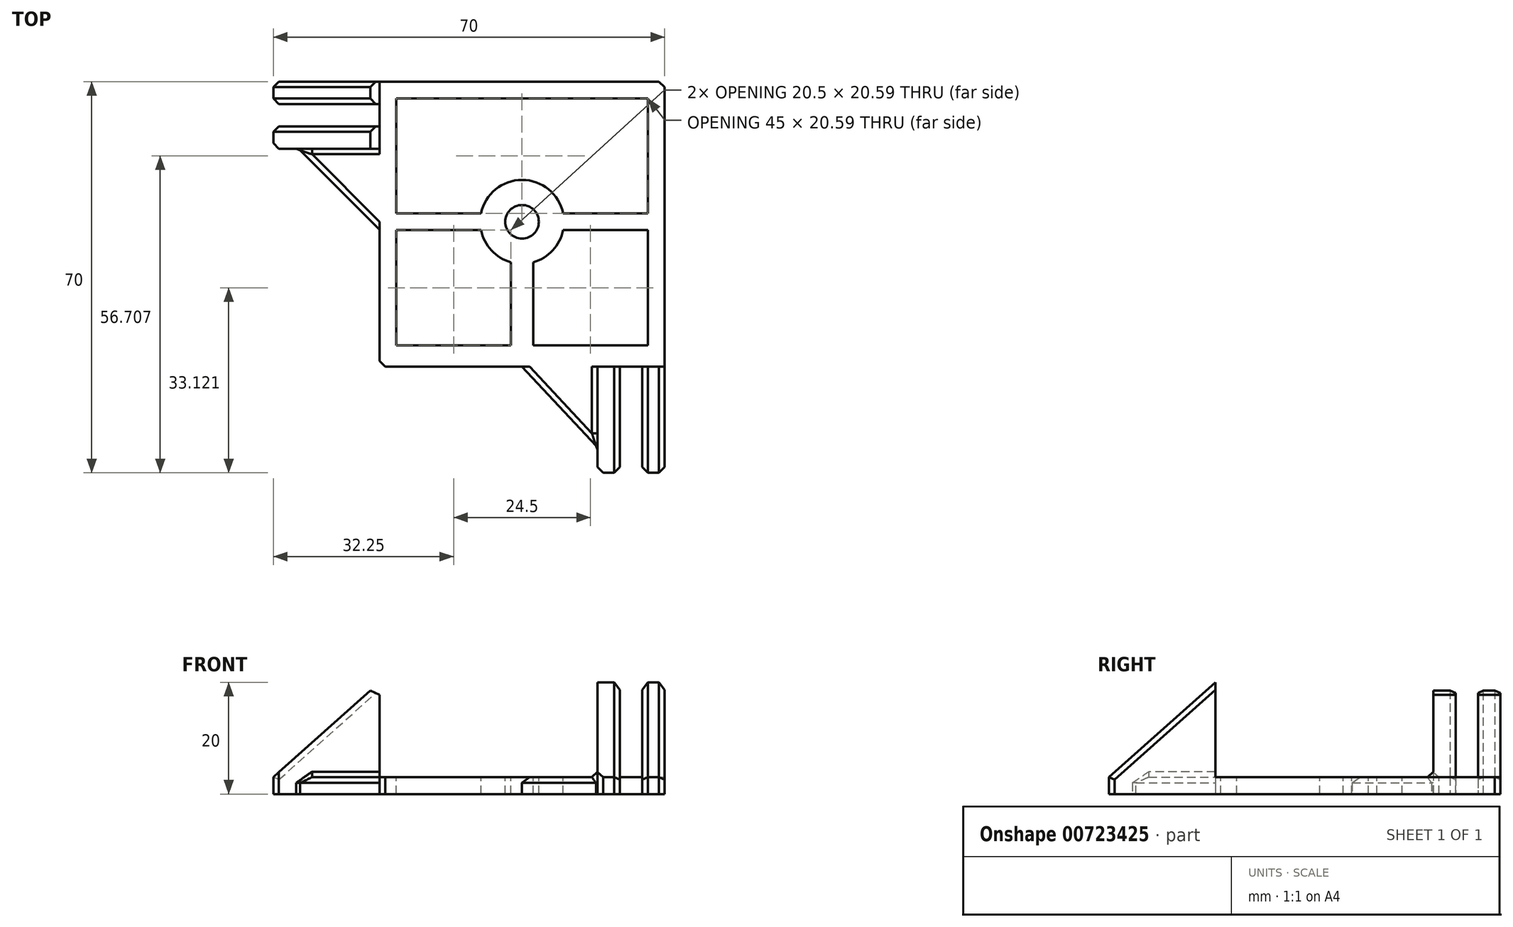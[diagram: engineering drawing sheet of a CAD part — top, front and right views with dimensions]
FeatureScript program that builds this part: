
annotation { "Feature Type Name" : "Feature", "Feature Type Description" : "" }
export const myFeature = defineFeature(function(context is Context, id is Id, definition is map)
    precondition{}
    {
        {
            var Q0;
            Q0=qCreatedBy(makeId("Top.planeOp"),FACE);
            var sketch = newSketch(context, id + "F0", { "sketchPlane" : qUnion([Q0])});
            skLineSegment(sketch, "E0.bottom", {"start": v(0, 0) * mm, "end": v(51, 0) * mm});
            skLineSegment(sketch, "E0.top", {"start": v(0, -51) * mm, "end": v(51, -51) * mm});
            skLineSegment(sketch, "E0.left", {"start": v(0, 0) * mm, "end": v(0, -51) * mm});
            skLineSegment(sketch, "E0.right", {"start": v(51, 0) * mm, "end": v(51, -51) * mm});
            skSolve(sketch);
        }
        {
            var Q0;
            Q0=qSketchRegion(id+"F0",true);
            extrude(context, id + "F1", {"entities" : qUnion([Q0]), "depth" : 3 * mm, "offsetDistance" : 25 * mm});
        }
        {
            var Q0;
            Q0=qCreatedBy(makeId("Top.planeOp"),FACE);
            var sketch = newSketch(context, id + "F2", { "sketchPlane" : qUnion([Q0])});
            skLineSegment(sketch, "E1", {"start": v(0, 0) * mm, "end": v(-19, 0) * mm});
            skLineSegment(sketch, "E2", {"start": v(-19, 0) * mm, "end": v(-19, -4) * mm});
            skLineSegment(sketch, "E3", {"start": v(-19, -4) * mm, "end": v(0, -4) * mm});
            skLineSegment(sketch, "E4", {"start": v(0, -4) * mm, "end": v(0, -8) * mm});
            skLineSegment(sketch, "E5", {"start": v(0, -8) * mm, "end": v(-19, -8) * mm});
            skLineSegment(sketch, "E6", {"start": v(-19, -8) * mm, "end": v(-19, -12) * mm});
            skLineSegment(sketch, "E7", {"start": v(-19, -12) * mm, "end": v(0, -12) * mm});
            skLineSegment(sketch, "E8", {"start": v(0, 0) * mm, "end": v(0, -12) * mm});
            skSolve(sketch);
        }
        {
            var Q0;
            Q0=qSketchRegion(id+"F2",true);
            extrude(context, id + "F3", {"entities" : qUnion([Q0]), "operationType" : NewBodyOperationType.ADD, "depth" : 20 * mm, "offsetDistance" : 25 * mm});
        }
        {
            var Q0;
            Q0=qCreatedBy(makeId("Top.planeOp"),FACE);
            var sketch = newSketch(context, id + "F4", { "sketchPlane" : qUnion([Q0])});
            skLineSegment(sketch, "E9", {"start": v(0, 0) * mm, "end": v(0, -11.5) * mm});
            skLineSegment(sketch, "E10", {"start": v(0, -11.5) * mm, "end": v(-15, -11.5) * mm});
            skLineSegment(sketch, "E11", {"start": v(0, -11.5) * mm, "end": v(0, -26.5) * mm});
            skLineSegment(sketch, "E12", {"start": v(0, -26.5) * mm, "end": v(-15, -11.5) * mm});
            skSolve(sketch);
        }
        {
            var Q0;
            Q0=makeQuery(id+"F4.imprint","IMPRINT",FACE,{"disambiguationData":[TD([[makeQuery(id+"F4.imprint","IMPRINT",EDGE,{"derivedFrom":sQuery(id+"F4.wireOp",EDGE,"E10")}),1.0]])]});
            extrude(context, id + "F5", {"entities" : qUnion([Q0]), "operationType" : NewBodyOperationType.ADD, "depth" : 3 * mm, "offsetDistance" : 25 * mm});
        }
        {
            var Q0;
            Q0=qCreatedBy(makeId("Top.planeOp"),FACE);
            var sketch = newSketch(context, id + "F6", { "sketchPlane" : qUnion([Q0])});
            skLineSegment(sketch, "E13", {"start": v(0, 0) * mm, "end": v(0, -51) * mm});
            skLineSegment(sketch, "E14", {"start": v(0, -51) * mm, "end": v(51, -51) * mm});
            skLineSegment(sketch, "E15", {"start": v(51, -51) * mm, "end": v(51, -70) * mm});
            skLineSegment(sketch, "E16", {"start": v(51, -70) * mm, "end": v(47, -70) * mm});
            skLineSegment(sketch, "E17", {"start": v(47, -70) * mm, "end": v(47, -51) * mm});
            skLineSegment(sketch, "E18", {"start": v(47, -51) * mm, "end": v(43, -51) * mm});
            skLineSegment(sketch, "E19", {"start": v(43, -51) * mm, "end": v(43, -70) * mm});
            skLineSegment(sketch, "E20", {"start": v(43, -70) * mm, "end": v(39, -70) * mm});
            skLineSegment(sketch, "E21", {"start": v(39, -70) * mm, "end": v(39, -51) * mm});
            skLineSegment(sketch, "E22", {"start": v(39, -51) * mm, "end": v(51, -51) * mm});
            skSolve(sketch);
        }
        {
            var Q0;
            Q0=qSketchRegion(id+"F6",true);
            extrude(context, id + "F7", {"entities" : qUnion([Q0]), "operationType" : NewBodyOperationType.ADD, "depth" : 20 * mm, "offsetDistance" : 25 * mm});
        }
        {
            var Q0;
            Q0=qCreatedBy(makeId("Top.planeOp"),FACE);
            var sketch = newSketch(context, id + "F8", { "sketchPlane" : qUnion([Q0])});
            skLineSegment(sketch, "E23", {"start": v(0, 0) * mm, "end": v(0, -51) * mm});
            skLineSegment(sketch, "E24", {"start": v(0, -51) * mm, "end": v(51, -51) * mm});
            skLineSegment(sketch, "E25", {"start": v(51, -51) * mm, "end": v(39.5, -51) * mm});
            skLineSegment(sketch, "E26", {"start": v(39.5, -51) * mm, "end": v(39.5, -66) * mm});
            skLineSegment(sketch, "E27", {"start": v(39.5, -66) * mm, "end": v(25.5, -51) * mm});
            skLineSegment(sketch, "E28", {"start": v(25.5, -51) * mm, "end": v(39.5, -51) * mm});
            skSolve(sketch);
        }
        {
            var Q0;
            Q0=qSketchRegion(id+"F8",true);
            extrude(context, id + "F9", {"entities" : qUnion([Q0]), "operationType" : NewBodyOperationType.ADD, "depth" : 3 * mm, "offsetDistance" : 25 * mm});
        }
        {
            var Q0;
            Q0=makeQuery(id+"F9.boolean.opBoolean","MERGE",FACE,{"derivedFrom":[makeQuery(id+"F5.boolean.opBoolean","MERGE",FACE,{"derivedFrom":[makeQuery(id+"F1.opExtrude","CAP_FACE",FACE,{"disambiguationData":[OSD([sQuery(id+"F0.wireOp",EDGE,"E0.bottom"),sQuery(id+"F0.wireOp",EDGE,"E0.top"),sQuery(id+"F0.wireOp",EDGE,"E0.left"),sQuery(id+"F0.wireOp",EDGE,"E0.right")])],"isStart":false}),makeQuery(id+"F5.opExtrude","CAP_FACE",FACE,{"disambiguationData":[OSD([sQuery(id+"F4.wireOp",EDGE,"E10"),sQuery(id+"F4.wireOp",EDGE,"E11"),sQuery(id+"F4.wireOp",EDGE,"E12")])],"isStart":false})]}),makeQuery(id+"F9.opExtrude","CAP_FACE",FACE,{"disambiguationData":[OSD([sQuery(id+"F8.wireOp",EDGE,"E26"),sQuery(id+"F8.wireOp",EDGE,"E27"),sQuery(id+"F8.wireOp",EDGE,"E28")])],"isStart":false})]});
            var sketch = newSketch(context, id + "F10", { "sketchPlane" : qUnion([Q0])});
            skCircle(sketch, "E29", {"center": v(25.5, -25.09) * mm, "radius": 3 * mm});
            skPoint(sketch, "E29.centerSnap0", {"position": v(25.5, 0) * mm});
            skSolve(sketch);
        }
        {
            var Q0;
            Q0 = qSketchRegion(id + "F10", true);
            extrude(context, id + "F11", {"entities" : qUnion([Q0]), "operationType" : NewBodyOperationType.REMOVE, "oppositeDirection" : true, "depth" : 25 * mm, "offsetDistance" : 25 * mm});
        }
        {
            var Q0;
            Q0=makeQuery(id+"F9.boolean.opBoolean","MERGE",FACE,{"derivedFrom":[makeQuery(id+"F5.boolean.opBoolean","MERGE",FACE,{"derivedFrom":[makeQuery(id+"F1.opExtrude","CAP_FACE",FACE,{"disambiguationData":[OSD([sQuery(id+"F0.wireOp",EDGE,"E0.bottom"),sQuery(id+"F0.wireOp",EDGE,"E0.top"),sQuery(id+"F0.wireOp",EDGE,"E0.left"),sQuery(id+"F0.wireOp",EDGE,"E0.right")])],"isStart":false}),makeQuery(id+"F5.opExtrude","CAP_FACE",FACE,{"disambiguationData":[OSD([sQuery(id+"F4.wireOp",EDGE,"E10"),sQuery(id+"F4.wireOp",EDGE,"E11"),sQuery(id+"F4.wireOp",EDGE,"E12")])],"isStart":false})]}),makeQuery(id+"F9.opExtrude","CAP_FACE",FACE,{"disambiguationData":[OSD([sQuery(id+"F8.wireOp",EDGE,"E26"),sQuery(id+"F8.wireOp",EDGE,"E27"),sQuery(id+"F8.wireOp",EDGE,"E28")])],"isStart":false})]});
            var sketch = newSketch(context, id + "F12", { "sketchPlane" : qUnion([Q0])});
            skCircle(sketch, "E30", {"center": v(25.5, -25.09) * mm, "radius": 7.5 * mm});
            skLineSegment(sketch, "E31", {"start": v(0, 0) * mm, "end": v(0, -3) * mm});
            skLineSegment(sketch, "E32", {"start": v(0, -3) * mm, "end": v(25.5, -3) * mm});
            skLineSegment(sketch, "E33", {"start": v(25.5, -3) * mm, "end": v(23.5, -3) * mm});
            skLineSegment(sketch, "E34", {"start": v(23.5, -3) * mm, "end": v(23.5, -17.86) * mm});
            skLineSegment(sketch, "E35", {"start": v(0, -3) * mm, "end": v(3, -3) * mm});
            skLineSegment(sketch, "E36", {"start": v(3, -3) * mm, "end": v(3, -25.09) * mm});
            skLineSegment(sketch, "E37", {"start": v(3, -25.09) * mm, "end": v(3, -23.59) * mm});
            skLineSegment(sketch, "E38", {"start": v(3, -23.59) * mm, "end": v(18.15, -23.59) * mm});
            skLineSegment(sketch, "E39", {"start": v(25.5, -25.09) * mm, "end": v(51, -25.09) * mm});
            skLineSegment(sketch, "E40", {"start": v(25.5, -25.09) * mm, "end": v(25.5, -51) * mm});
            skLineSegment(sketch, "E41.MirrorCS", {"start": v(3, -26.59) * mm, "end": v(18.15, -26.59) * mm});
            skLineSegment(sketch, "E42.MirrorCS", {"start": v(3, -47.17) * mm, "end": v(3, -25.09) * mm});
            skLineSegment(sketch, "E43.MirrorCS", {"start": v(0, -47.17) * mm, "end": v(25.5, -47.17) * mm});
            skLineSegment(sketch, "E44.MirrorCS", {"start": v(23.5, -47.17) * mm, "end": v(23.5, -32.31) * mm});
            skLineSegment(sketch, "E45.MirrorCS", {"start": v(27.5, -47.17) * mm, "end": v(27.5, -32.31) * mm});
            skLineSegment(sketch, "E46.MirrorCS", {"start": v(51, -47.17) * mm, "end": v(25.5, -47.17) * mm});
            skLineSegment(sketch, "E47.MirrorCS", {"start": v(48, -47.17) * mm, "end": v(48, -25.09) * mm});
            skLineSegment(sketch, "E48.MirrorCS", {"start": v(48, -26.59) * mm, "end": v(32.85, -26.59) * mm});
            skLineSegment(sketch, "E49.MirrorCS", {"start": v(48, -23.59) * mm, "end": v(32.85, -23.59) * mm});
            skLineSegment(sketch, "E50.MirrorCS", {"start": v(48, -3) * mm, "end": v(48, -25.09) * mm});
            skLineSegment(sketch, "E51.MirrorCS", {"start": v(51, -3) * mm, "end": v(25.5, -3) * mm});
            skLineSegment(sketch, "E52.MirrorCS", {"start": v(27.5, -3) * mm, "end": v(27.5, -17.86) * mm});
            skSolve(sketch);
        }
        {
            var Q0;
            {var subQ4=sQuery(id+"F12.wireOp",EDGE,"E49.MirrorCS");Q0=makeQuery(id+"F12.imprint","IMPRINT",FACE,{"disambiguationData":[TD([[makeQuery(id+"F12.imprint","IMPRINT",EDGE,{"derivedFrom":subQ4}),-1.0]])]});}
            var Q1;
            {var subQ4=sQuery(id+"F12.wireOp",EDGE,"E45.MirrorCS");Q1=makeQuery(id+"F12.imprint","IMPRINT",FACE,{"disambiguationData":[TD([[makeQuery(id+"F12.imprint","IMPRINT",EDGE,{"derivedFrom":subQ4}),-1.0]])]});}
            var Q2;
            Q2=makeQuery(id+"F12.imprint","IMPRINT",FACE,{"disambiguationData":[TD([[makeQuery(id+"F12.imprint","IMPRINT",EDGE,{"derivedFrom":sQuery(id+"F12.wireOp",EDGE,"E32")}),-1.0]])]});
            var Q3;
            {var subQ1=sQuery(id+"F12.wireOp",EDGE,"E41.MirrorCS");Q3=makeQuery(id+"F12.imprint","IMPRINT",FACE,{"disambiguationData":[TD([[makeQuery(id+"F12.imprint","IMPRINT",EDGE,{"derivedFrom":subQ1}),-1.0]])]});}
            extrude(context, id + "F13", {"entities" : qUnion([Q0, Q1, Q2, Q3]), "operationType" : NewBodyOperationType.REMOVE, "oppositeDirection" : true, "depth" : 25 * mm, "offsetDistance" : 25 * mm});
        }
        {
            var Q0;
            Q0=makeQuery(id+"F3.opExtrude","SWEPT_FACE",FACE,{"disambiguationData":[OSD([sQuery(id+"F2.wireOp",EDGE,"E7")])]});
            var sketch = newSketch(context, id + "F14", { "sketchPlane" : qUnion([Q0])});
            skLineSegment(sketch, "E53", {"start": v(-19, 3) * mm, "end": v(0, 20) * mm});
            skLineSegment(sketch, "E54", {"start": v(0, 20) * mm, "end": v(-19, 20) * mm});
            skLineSegment(sketch, "E55", {"start": v(-19, 20) * mm, "end": v(-19, 3) * mm});
            skSolve(sketch);
        }
        {
            var Q0;
            Q0 = qSketchRegion(id + "F14", true);
            extrude(context, id + "F15", {"entities" : qUnion([Q0]), "operationType" : NewBodyOperationType.REMOVE, "oppositeDirection" : true, "depth" : 25 * mm, "offsetDistance" : 25 * mm});
        }
        {
            var Q0;
            Q0=makeQuery(id+"F7.opExtrude","SWEPT_FACE",FACE,{"disambiguationData":[OSD([sQuery(id+"F6.wireOp",EDGE,"E21")])]});
            var sketch = newSketch(context, id + "F16", { "sketchPlane" : qUnion([Q0])});
            skLineSegment(sketch, "E56", {"start": v(70, 3) * mm, "end": v(51, 20) * mm});
            skLineSegment(sketch, "E57", {"start": v(51, 20) * mm, "end": v(70, 20) * mm});
            skLineSegment(sketch, "E58", {"start": v(70, 20) * mm, "end": v(70, 3) * mm});
            skSolve(sketch);
        }
        {
            var Q0;
            Q0 = qSketchRegion(id + "F16", true);
            extrude(context, id + "F17", {"entities" : qUnion([Q0]), "operationType" : NewBodyOperationType.REMOVE, "oppositeDirection" : true, "depth" : 25 * mm, "offsetDistance" : 25 * mm});
        }
        {
            var Q0;
            Q0 = qSketchRegion(id + "F16", true);
            extrude(context, id + "F18", {"entities" : qUnion([Q0]), "operationType" : NewBodyOperationType.REMOVE, "oppositeDirection" : true, "depth" : 25 * mm, "offsetDistance" : 25 * mm});
        }
        {
            var Q0;
            Q0=makeQuery(id+"F15.boolean.opBoolean","INTERSECT",EDGE,{"derivedFrom":[makeQuery(id+"F3.boolean.opBoolean","MERGE",FACE,{"derivedFrom":[makeQuery(id+"F1.opExtrude","SWEPT_FACE",FACE,{"disambiguationData":[OSD([sQuery(id+"F0.wireOp",EDGE,"E0.bottom")])]}),makeQuery(id+"F3.opExtrude","SWEPT_FACE",FACE,{"disambiguationData":[OSD([sQuery(id+"F2.wireOp",EDGE,"E1")])]})]}),makeQuery(id+"F15.opExtrude","SWEPT_FACE",FACE,{"disambiguationData":[OSD([sQuery(id+"F14.wireOp",EDGE,"E53")])]})]});
            var Q1;
            Q1=makeQuery(id+"F15.boolean.opBoolean","INTERSECT",EDGE,{"derivedFrom":[makeQuery(id+"F3.opExtrude","SWEPT_FACE",FACE,{"disambiguationData":[OSD([sQuery(id+"F2.wireOp",EDGE,"E3")])]}),makeQuery(id+"F15.opExtrude","SWEPT_FACE",FACE,{"disambiguationData":[OSD([sQuery(id+"F14.wireOp",EDGE,"E53")])]})]});
            var Q2;
            {var subQ0=sQuery(id+"F2.wireOp",EDGE,"E8");Q2=makeQuery(id+"F15.boolean.opBoolean","MERGE",EDGE,{"derivedFrom":[makeQuery(id+"F3.opExtrude","CAP_EDGE",EDGE,{"disambiguationData":[OSD([subQ0]),TDD([makeQuery(id+"F2.imprint","IMPRINT",EDGE,{"disambiguationData":[TD([[makeQuery(id+"F2.imprint","INTERSECT",VERTEX,{"derivedFrom":[sQuery(id+"F2.wireOp",EDGE,"E1"),subQ0]}),-1.0]])],"derivedFrom":subQ0})])],"isStart":false}),makeQuery(id+"F15.opExtrude","SWEPT_EDGE",EDGE,{"disambiguationData":[OSD([sQuery(id+"F2.wireOp",EDGE,"E7"),subQ0,sQuery(id+"F14.wireOp",EDGE,"E53"),sQuery(id+"F14.wireOp",EDGE,"E54")])]})]});}
            var Q3;
            {var subQ0=sQuery(id+"F2.wireOp",EDGE,"E8");var subQ1=sQuery(id+"F2.wireOp",EDGE,"E7");Q3=makeQuery(id+"F15.boolean.opBoolean","MERGE",EDGE,{"derivedFrom":[makeQuery(id+"F3.opExtrude","CAP_EDGE",EDGE,{"disambiguationData":[OSD([subQ0]),TDD([makeQuery(id+"F2.imprint","IMPRINT",EDGE,{"disambiguationData":[TD([[makeQuery(id+"F2.imprint","INTERSECT",VERTEX,{"derivedFrom":[sQuery(id+"F2.wireOp",EDGE,"E5"),subQ0]}),-1.0]])],"derivedFrom":subQ0})])],"isStart":false}),makeQuery(id+"F15.opExtrude","SWEPT_EDGE",EDGE,{"disambiguationData":[OSD([subQ1,subQ0,sQuery(id+"F14.wireOp",EDGE,"E53"),sQuery(id+"F14.wireOp",EDGE,"E54")])]})]});}
            var Q4;
            Q4=makeQuery(id+"F15.boolean.opBoolean","INTERSECT",EDGE,{"derivedFrom":[makeQuery(id+"F3.opExtrude","SWEPT_FACE",FACE,{"disambiguationData":[OSD([sQuery(id+"F2.wireOp",EDGE,"E5")])]}),makeQuery(id+"F15.opExtrude","SWEPT_FACE",FACE,{"disambiguationData":[OSD([sQuery(id+"F14.wireOp",EDGE,"E53")])]})]});
            var Q5;
            Q5=makeQuery(id+"F15.boolean.opBoolean","COPY",EDGE,{"derivedFrom":makeQuery(id+"F15.opExtrude","CAP_EDGE",EDGE,{"disambiguationData":[OSD([sQuery(id+"F14.wireOp",EDGE,"E53")])],"isStart":true})});
            var Q6;
            {var subQ0=sQuery(id+"F2.wireOp",EDGE,"E6");var subQ1=sQuery(id+"F14.wireOp",EDGE,"E53");Q6=makeQuery(id+"F15.boolean.opBoolean","COPY",EDGE,{"disambiguationData":[topologyDisambiguationEdgeConnected([makeQuery(id+"F3.opExtrude","SWEPT_FACE",FACE,{"disambiguationData":[OSD([subQ0])]})])],"derivedFrom":makeQuery(id+"F15.opExtrude","SWEPT_EDGE",EDGE,{"disambiguationData":[OSD([subQ0,sQuery(id+"F2.wireOp",EDGE,"E7"),subQ1,sQuery(id+"F14.wireOp",EDGE,"E55")])]})});}
            var Q7;
            {var subQ0=sQuery(id+"F14.wireOp",EDGE,"E53");Q7=makeQuery(id+"F15.boolean.opBoolean","COPY",EDGE,{"disambiguationData":[topologyDisambiguationEdgeConnected([makeQuery(id+"F3.opExtrude","SWEPT_FACE",FACE,{"disambiguationData":[OSD([sQuery(id+"F2.wireOp",EDGE,"E2")])]})])],"derivedFrom":makeQuery(id+"F15.opExtrude","SWEPT_EDGE",EDGE,{"disambiguationData":[OSD([sQuery(id+"F2.wireOp",EDGE,"E6"),sQuery(id+"F2.wireOp",EDGE,"E7"),subQ0,sQuery(id+"F14.wireOp",EDGE,"E55")])]})});}
            var Q8;
            Q8=makeQuery(id+"F5.opExtrude","CAP_EDGE",EDGE,{"disambiguationData":[OSD([sQuery(id+"F4.wireOp",EDGE,"E12")])],"isStart":false});
            var Q9;
            Q9=makeQuery(id+"F5.boolean.opBoolean","INTERSECT",EDGE,{"derivedFrom":[makeQuery(id+"F3.opExtrude","SWEPT_FACE",FACE,{"disambiguationData":[OSD([sQuery(id+"F2.wireOp",EDGE,"E7")])]}),makeQuery(id+"F5.opExtrude","CAP_FACE",FACE,{"disambiguationData":[OSD([sQuery(id+"F4.wireOp",EDGE,"E10"),sQuery(id+"F4.wireOp",EDGE,"E11"),sQuery(id+"F4.wireOp",EDGE,"E12")])],"isStart":false})]});
            var Q10;
            Q10=makeQuery(id+"F9.opExtrude","CAP_EDGE",EDGE,{"disambiguationData":[OSD([sQuery(id+"F8.wireOp",EDGE,"E27")])],"isStart":false});
            var Q11;
            Q11=makeQuery(id+"F9.boolean.opBoolean","INTERSECT",EDGE,{"derivedFrom":[makeQuery(id+"F7.opExtrude","SWEPT_FACE",FACE,{"disambiguationData":[OSD([sQuery(id+"F6.wireOp",EDGE,"E21")])]}),makeQuery(id+"F9.opExtrude","CAP_FACE",FACE,{"disambiguationData":[OSD([sQuery(id+"F8.wireOp",EDGE,"E26"),sQuery(id+"F8.wireOp",EDGE,"E27"),sQuery(id+"F8.wireOp",EDGE,"E28")])],"isStart":false})]});
            var Q12;
            Q12=makeQuery(id+"F7.opExtrude","SWEPT_EDGE",EDGE,{"disambiguationData":[OSD([sQuery(id+"F6.wireOp",EDGE,"E20"),sQuery(id+"F6.wireOp",EDGE,"E21")])]});
            var Q13;
            Q13=makeQuery(id+"F7.opExtrude","SWEPT_EDGE",EDGE,{"disambiguationData":[OSD([sQuery(id+"F6.wireOp",EDGE,"E19"),sQuery(id+"F6.wireOp",EDGE,"E20")])]});
            var Q14;
            Q14=makeQuery(id+"F7.opExtrude","SWEPT_EDGE",EDGE,{"disambiguationData":[OSD([sQuery(id+"F6.wireOp",EDGE,"E16"),sQuery(id+"F6.wireOp",EDGE,"E17")])]});
            var Q15;
            Q15=makeQuery(id+"F7.opExtrude","SWEPT_EDGE",EDGE,{"disambiguationData":[OSD([sQuery(id+"F6.wireOp",EDGE,"E15"),sQuery(id+"F6.wireOp",EDGE,"E16")])]});
            var Q16;
            {var subQ0=sQuery(id+"F16.wireOp",EDGE,"E56");Q16=makeQuery(id+"F17.boolean.opBoolean","COPY",EDGE,{"disambiguationData":[topologyDisambiguationEdgeConnected([makeQuery(id+"F7.opExtrude","SWEPT_FACE",FACE,{"disambiguationData":[OSD([sQuery(id+"F6.wireOp",EDGE,"E16")])]})])],"derivedFrom":makeQuery(id+"F17.opExtrude","SWEPT_EDGE",EDGE,{"disambiguationData":[OSD([sQuery(id+"F6.wireOp",EDGE,"E20"),sQuery(id+"F6.wireOp",EDGE,"E21"),subQ0,sQuery(id+"F16.wireOp",EDGE,"E58")])]})});}
            var Q17;
            {var subQ0=sQuery(id+"F6.wireOp",EDGE,"E20");var subQ1=sQuery(id+"F16.wireOp",EDGE,"E56");Q17=makeQuery(id+"F17.boolean.opBoolean","COPY",EDGE,{"disambiguationData":[topologyDisambiguationEdgeConnected([makeQuery(id+"F7.opExtrude","SWEPT_FACE",FACE,{"disambiguationData":[OSD([subQ0])]})])],"derivedFrom":makeQuery(id+"F17.opExtrude","SWEPT_EDGE",EDGE,{"disambiguationData":[OSD([subQ0,sQuery(id+"F6.wireOp",EDGE,"E21"),subQ1,sQuery(id+"F16.wireOp",EDGE,"E58")])]})});}
            var Q18;
            {var subQ0=sQuery(id+"F6.wireOp",EDGE,"E22");var subQ1=sQuery(id+"F6.wireOp",EDGE,"E21");Q18=makeQuery(id+"F17.boolean.opBoolean","MERGE",EDGE,{"derivedFrom":[makeQuery(id+"F7.opExtrude","CAP_EDGE",EDGE,{"disambiguationData":[OSD([subQ0]),TDD([makeQuery(id+"F6.imprint","IMPRINT",EDGE,{"disambiguationData":[TD([[makeQuery(id+"F6.imprint","INTERSECT",VERTEX,{"derivedFrom":[subQ1,subQ0]}),-1.0]])],"derivedFrom":subQ0})])],"isStart":false}),makeQuery(id+"F17.opExtrude","SWEPT_EDGE",EDGE,{"disambiguationData":[OSD([subQ1,subQ0,sQuery(id+"F16.wireOp",EDGE,"E56"),sQuery(id+"F16.wireOp",EDGE,"E57")])]})]});}
            var Q19;
            Q19=makeQuery(id+"F3.opExtrude","SWEPT_EDGE",EDGE,{"disambiguationData":[OSD([sQuery(id+"F2.wireOp",EDGE,"E6"),sQuery(id+"F2.wireOp",EDGE,"E7")])]});
            var Q20;
            Q20=makeQuery(id+"F3.opExtrude","SWEPT_EDGE",EDGE,{"disambiguationData":[OSD([sQuery(id+"F2.wireOp",EDGE,"E5"),sQuery(id+"F2.wireOp",EDGE,"E6")])]});
            var Q21;
            Q21=makeQuery(id+"F3.opExtrude","SWEPT_EDGE",EDGE,{"disambiguationData":[OSD([sQuery(id+"F2.wireOp",EDGE,"E2"),sQuery(id+"F2.wireOp",EDGE,"E3")])]});
            var Q22;
            Q22=makeQuery(id+"F3.opExtrude","SWEPT_EDGE",EDGE,{"disambiguationData":[OSD([sQuery(id+"F2.wireOp",EDGE,"E1"),sQuery(id+"F2.wireOp",EDGE,"E2")])]});
            var Q23;
            {var subQ0=sQuery(id+"F6.wireOp",EDGE,"E22");Q23=makeQuery(id+"F17.boolean.opBoolean","MERGE",EDGE,{"derivedFrom":[makeQuery(id+"F7.opExtrude","CAP_EDGE",EDGE,{"disambiguationData":[OSD([subQ0]),TDD([makeQuery(id+"F6.imprint","IMPRINT",EDGE,{"disambiguationData":[TD([[makeQuery(id+"F6.imprint","INTERSECT",VERTEX,{"derivedFrom":[sQuery(id+"F6.wireOp",EDGE,"E15"),subQ0]}),1.0]])],"derivedFrom":subQ0})])],"isStart":false}),makeQuery(id+"F17.opExtrude","SWEPT_EDGE",EDGE,{"disambiguationData":[OSD([sQuery(id+"F6.wireOp",EDGE,"E21"),subQ0,sQuery(id+"F16.wireOp",EDGE,"E56"),sQuery(id+"F16.wireOp",EDGE,"E57")])]})]});}
            var Q24;
            Q24=makeQuery(id+"F17.boolean.opBoolean","INTERSECT",EDGE,{"derivedFrom":[makeQuery(id+"F7.opExtrude","SWEPT_FACE",FACE,{"disambiguationData":[OSD([sQuery(id+"F6.wireOp",EDGE,"E17")])]}),makeQuery(id+"F17.opExtrude","SWEPT_FACE",FACE,{"disambiguationData":[OSD([sQuery(id+"F16.wireOp",EDGE,"E56")])]})]});
            var Q25;
            Q25=makeQuery(id+"F17.boolean.opBoolean","INTERSECT",EDGE,{"derivedFrom":[makeQuery(id+"F7.boolean.opBoolean","MERGE",FACE,{"derivedFrom":[makeQuery(id+"F1.opExtrude","SWEPT_FACE",FACE,{"disambiguationData":[OSD([sQuery(id+"F0.wireOp",EDGE,"E0.right")])]}),makeQuery(id+"F7.opExtrude","SWEPT_FACE",FACE,{"disambiguationData":[OSD([sQuery(id+"F6.wireOp",EDGE,"E15")])]})]}),makeQuery(id+"F17.opExtrude","SWEPT_FACE",FACE,{"disambiguationData":[OSD([sQuery(id+"F16.wireOp",EDGE,"E56")])]})]});
            var Q26;
            Q26=makeQuery(id+"F17.boolean.opBoolean","INTERSECT",EDGE,{"derivedFrom":[makeQuery(id+"F7.opExtrude","SWEPT_FACE",FACE,{"disambiguationData":[OSD([sQuery(id+"F6.wireOp",EDGE,"E19")])]}),makeQuery(id+"F17.opExtrude","SWEPT_FACE",FACE,{"disambiguationData":[OSD([sQuery(id+"F16.wireOp",EDGE,"E56")])]})]});
            var Q27;
            Q27=makeQuery(id+"F17.boolean.opBoolean","COPY",EDGE,{"derivedFrom":makeQuery(id+"F17.opExtrude","CAP_EDGE",EDGE,{"disambiguationData":[OSD([sQuery(id+"F16.wireOp",EDGE,"E56")])],"isStart":true})});
            var Q28;
            Q28=makeQuery(id+"F1.opExtrude","SWEPT_EDGE",EDGE,{"disambiguationData":[OSD([sQuery(id+"F0.wireOp",EDGE,"E0.top"),sQuery(id+"F0.wireOp",EDGE,"E0.left")])]});
            var Q29;
            Q29=makeQuery(id+"F5.opExtrude","SWEPT_EDGE",EDGE,{"disambiguationData":[OSD([sQuery(id+"F4.wireOp",EDGE,"E11"),sQuery(id+"F4.wireOp",EDGE,"E12")])]});
            var Q30;
            Q30=makeQuery(id+"F9.opExtrude","SWEPT_EDGE",EDGE,{"disambiguationData":[OSD([sQuery(id+"F8.wireOp",EDGE,"E27"),sQuery(id+"F8.wireOp",EDGE,"E28")])]});
            var Q31;
            Q31=makeQuery(id+"F1.opExtrude","SWEPT_EDGE",EDGE,{"disambiguationData":[OSD([sQuery(id+"F0.wireOp",EDGE,"E0.bottom"),sQuery(id+"F0.wireOp",EDGE,"E0.right")])]});
            chamfer(context, id + "F19", {"entities" : qUnion([Q0, Q1, Q2, Q3, Q4, Q5, Q6, Q7, Q8, Q9, Q10, Q11, Q12, Q13, Q14, Q15, Q16, Q17, Q18, Q19, Q20, Q21, Q22, Q23, Q24, Q25, Q26, Q27, Q28, Q29, Q30, Q31]), "width" : 1 * mm, "tangentPropagation" : true});
        }
    });
